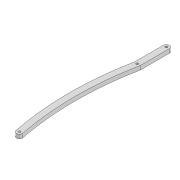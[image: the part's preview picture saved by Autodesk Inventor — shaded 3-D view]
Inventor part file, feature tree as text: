
AUTODESK INVENTOR PART (.ipt)
format: ipt  version: 2022 (Build 260153000, 153)  size: 99,840 bytes
history: native  units: mm
features: extrude x1, sketch x1
ambient origin geometry x8: Origin, YZ Plane, XZ Plane, XY Plane, X Axis, Y Axis, Z Axis, Center Point
bodies: Solid1 (feature_tree)
feature tree (2):
  extrude  "Extrusion1"  Depth=300.0mm
  sketch  "Sketch1"  dims[d0=2.2mm d1=2.2mm d2=6.0mm d3=146.336mm d6=4.0mm d7=0.0mm d14=2.2mm d15=117.27mm d16=300.0mm d17=300.0mm]
